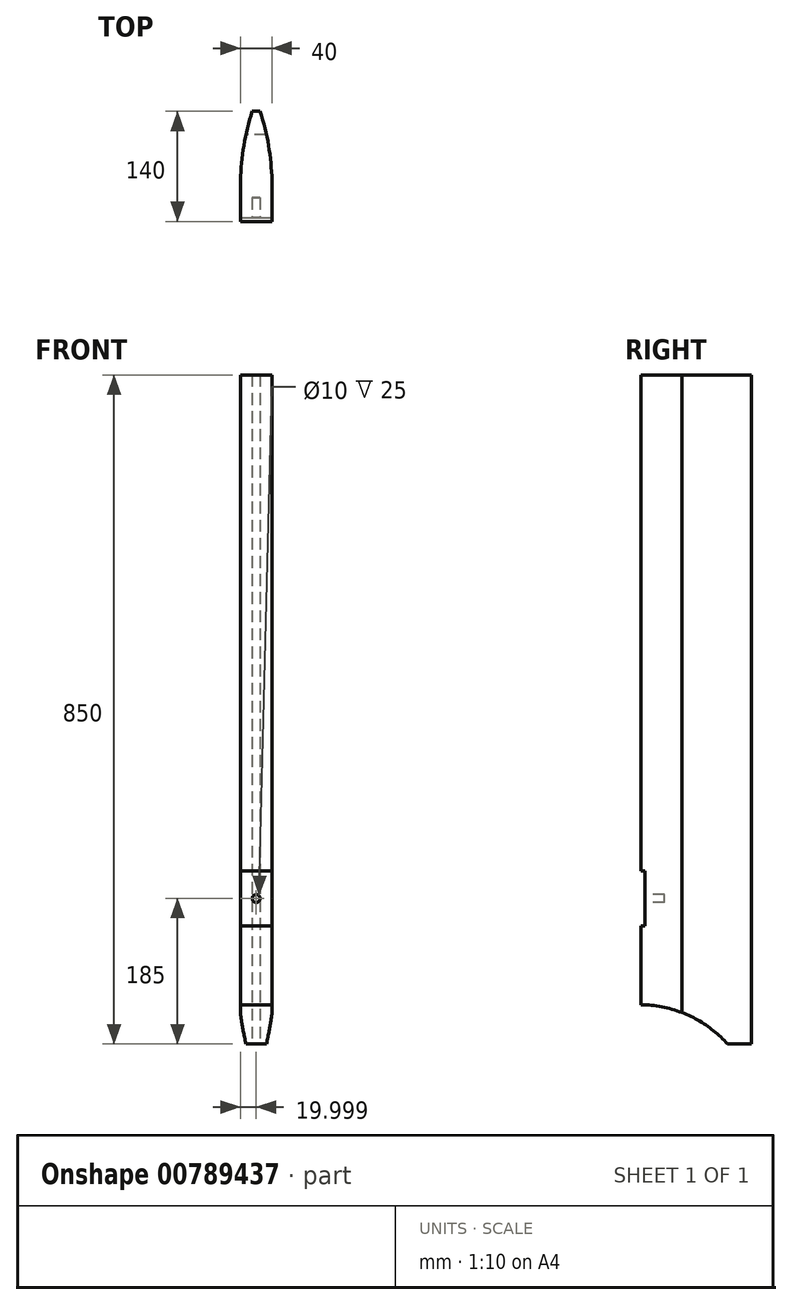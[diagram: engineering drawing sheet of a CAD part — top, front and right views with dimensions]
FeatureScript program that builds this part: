
annotation { "Feature Type Name" : "Feature", "Feature Type Description" : "" }
export const myFeature = defineFeature(function(context is Context, id is Id, definition is map)
    precondition{}
    {
        {
            var Q0;
            Q0=qCreatedBy(makeId("Top.planeOp"),FACE);
            var sketch = newSketch(context, id + "F0", { "sketchPlane" : qUnion([Q0])});
            skLineSegment(sketch, "E0.bottom", {"start": v(39.4, -4.32) * mm, "end": v(49.4, -4.32) * mm});
            skLineSegment(sketch, "E0.top", {"start": v(24.4, -144.32) * mm, "end": v(64.4, -144.32) * mm});
            skLineSegment(sketch, "E0.left", {"start": v(24.4, -92.26) * mm, "end": v(24.4, -144.32) * mm});
            skLineSegment(sketch, "E0.right", {"start": v(64.4, -92.26) * mm, "end": v(64.4, -144.32) * mm});
            skArc(sketch, "E1", {"start": v(39.4, -4.32) * mm, "mid": v(27.57, -54.82) * mm, "end": v(24.4, -106.58) * mm});
            skArc(sketch, "E2.MirrorCS", {"start": v(49.4, -4.32) * mm, "mid": v(61.23, -54.82) * mm, "end": v(64.4, -106.58) * mm});
            skPoint(sketch, "E3.orphan", {"position": v(24.4, -4.32) * mm});
            skPoint(sketch, "E4.orphan", {"position": v(64.4, -4.32) * mm});
            skPoint(sketch, "E5.end.orphan", {"position": v(44.4, -144.32) * mm});
            skPoint(sketch, "E5.start.orphan", {"position": v(44.4, -4.32) * mm});
            skSolve(sketch);
        }
        {
            var Q0;
            {var subQ5=sQuery(id+"F0.wireOp",EDGE,"E0.bottom");Q0=makeQuery(id+"F0.imprint","IMPRINT",FACE,{"disambiguationData":[TD([[makeQuery(id+"F0.imprint","IMPRINT",EDGE,{"derivedFrom":subQ5}),-1.0]])]});}
            extrude(context, id + "F1", {"entities" : qUnion([Q0]), "depth" : 850 * mm, "offsetDistance" : 25 * mm});
        }
        {
            var Q0;
            Q0=makeQuery(id+"F1.opExtrude","SWEPT_FACE",FACE,{"disambiguationData":[OSD([sQuery(id+"F0.wireOp",EDGE,"E0.top")])]});
            var sketch = newSketch(context, id + "F2", { "sketchPlane" : qUnion([Q0])});
            skLineSegment(sketch, "E6.bottom", {"start": v(24.4, 150) * mm, "end": v(64.4, 150) * mm});
            skLineSegment(sketch, "E6.top", {"start": v(24.4, 220) * mm, "end": v(64.4, 220) * mm});
            skLineSegment(sketch, "E6.left", {"start": v(24.4, 150) * mm, "end": v(24.4, 220) * mm});
            skLineSegment(sketch, "E6.right", {"start": v(64.4, 150) * mm, "end": v(64.4, 220) * mm});
            skSolve(sketch);
        }
        {
            var Q0;
            Q0=makeQuery(id+"F2.imprint","IMPRINT",FACE,{"disambiguationData":[TD([[makeQuery(id+"F2.imprint","IMPRINT",EDGE,{"derivedFrom":sQuery(id+"F2.wireOp",EDGE,"E6.bottom")}),1.0]])]});
            extrude(context, id + "F3", {"entities" : qUnion([Q0]), "operationType" : NewBodyOperationType.REMOVE, "oppositeDirection" : true, "depth" : 5 * mm, "offsetDistance" : 25 * mm});
        }
        {
            var Q0;
            Q0=makeQuery(id+"F3.boolean.opBoolean","COPY",FACE,{"derivedFrom":makeQuery(id+"F3.opExtrude","CAP_FACE",FACE,{"disambiguationData":[OSD([sQuery(id+"F2.wireOp",EDGE,"E6.bottom"),sQuery(id+"F2.wireOp",EDGE,"E6.top"),sQuery(id+"F2.wireOp",EDGE,"E6.left"),sQuery(id+"F2.wireOp",EDGE,"E6.right")])],"isStart":false})});
            var sketch = newSketch(context, id + "F4", { "sketchPlane" : qUnion([Q0])});
            skCircle(sketch, "E7", {"center": v(44.4, 185) * mm, "radius": 5 * mm});
            skPoint(sketch, "E7.centerSnap0", {"position": v(44.4, 220) * mm});
            skSolve(sketch);
        }
        {
            var Q0;
            Q0=makeQuery(id+"F4.imprint","IMPRINT",FACE,{"disambiguationData":[TD([[makeQuery(id+"F4.imprint","IMPRINT",EDGE,{"derivedFrom":sQuery(id+"F4.wireOp",EDGE,"E7")}),1.0]])]});
            extrude(context, id + "F5", {"entities" : qUnion([Q0]), "operationType" : NewBodyOperationType.REMOVE, "oppositeDirection" : true, "depth" : 25 * mm, "offsetDistance" : 25 * mm});
        }
        {
            var Q0;
            Q0=qCreatedBy(makeId("Right.planeOp"),FACE);
            var sketch = newSketch(context, id + "F6", { "sketchPlane" : qUnion([Q0])});
            skArc(sketch, "E8", {"start": v(-34.32, 0) * mm, "mid": v(-84.06, 36.57) * mm, "end": v(-144.32, 50) * mm});
            skLineSegment(sketch, "E9", {"start": v(-144.32, 50) * mm, "end": v(-144.32, 0) * mm});
            skLineSegment(sketch, "E10", {"start": v(-34.32, 0) * mm, "end": v(-144.32, 0) * mm});
            skSolve(sketch);
        }
        {
            var Q0;
            Q0=makeQuery(id+"F6.imprint","IMPRINT",FACE,{"disambiguationData":[TD([[makeQuery(id+"F6.imprint","IMPRINT",EDGE,{"derivedFrom":sQuery(id+"F6.wireOp",EDGE,"E8")}),1.0]])]});
            extrude(context, id + "F7", {"entities" : qUnion([Q0]), "operationType" : NewBodyOperationType.REMOVE, "depth" : 150 * mm, "offsetDistance" : 25 * mm});
        }
    });
